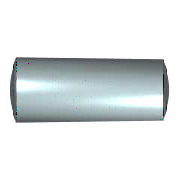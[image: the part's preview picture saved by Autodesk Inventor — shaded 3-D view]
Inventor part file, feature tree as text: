
AUTODESK INVENTOR PART (.ipt)
format: ipt  version: 2017 SP1 (Build 210196100, 196)  size: 119,296 bytes
history: native  units: mm (DEFAULTED — no unit token found)
features: sketch x1
ambient origin geometry x8: Origin, YZ Plane, XZ Plane, XY Plane, X Axis, Y Axis, Z Axis, Center Point
bodies: Solid1 (feature_tree), Body (feature_tree)
feature tree (1):
  sketch  "Sketch1"  dims[d0=3.184589mm d1=3.61442mm d2=19.05mm d3=3.5814mm d4=3.5814mm d5=90.0deg d8=0.373437mm d9=0.489407mm d17=0.0mm d18=0.0mm d19=0.0mm]
